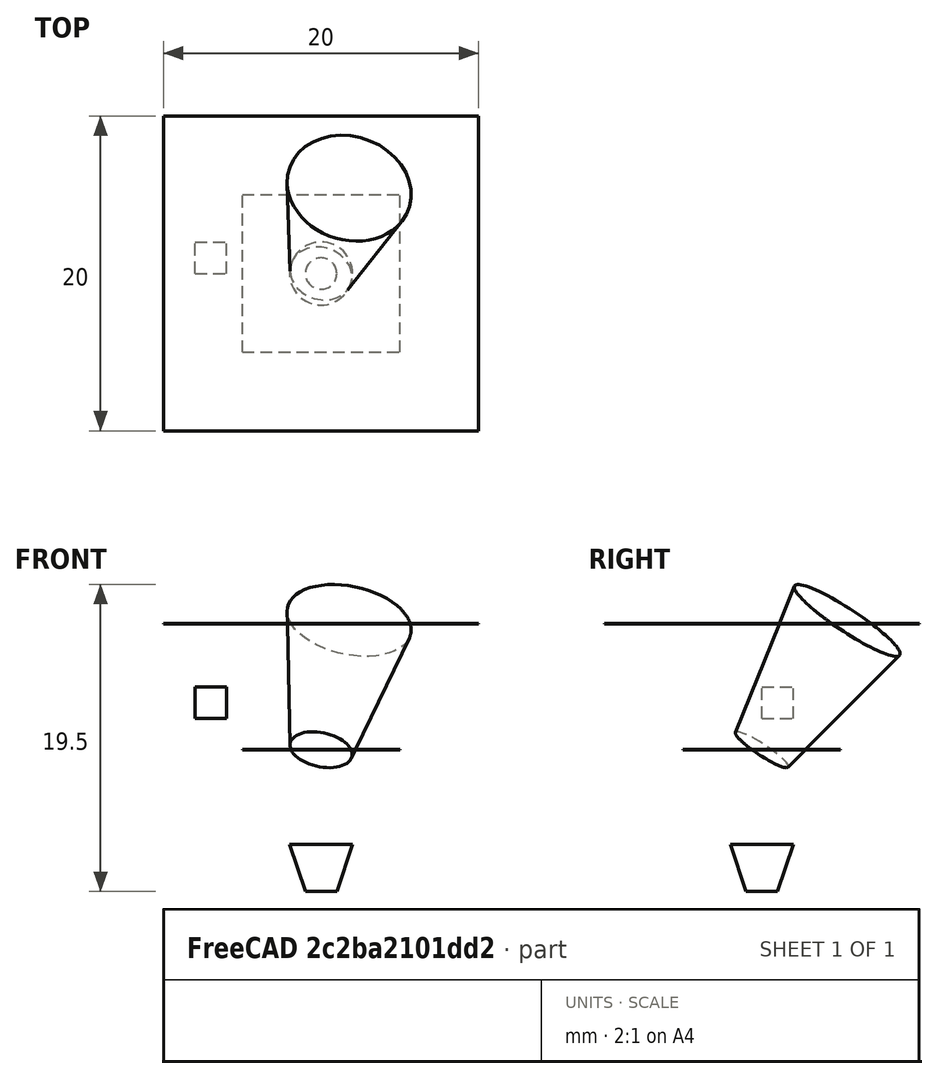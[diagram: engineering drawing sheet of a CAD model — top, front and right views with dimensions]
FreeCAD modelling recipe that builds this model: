
FCSTD DOCUMENT  (FreeCAD 0.16R5332 (Git))
Label: clipping
License: All rights reserved
LicenseURL: http://en.wikipedia.org/wiki/All_rights_reserved
objects: Raytracing::RayFeature×5, Raytracing::LuxFeature×5, Part::Box×3, Part::Cone×2, Raytracing::RayProject×1, Raytracing::LuxProject×1
note: 5 computed .brp shape members not serialized (recipe doc carries the construction recipe); baked Part::Feature solids carry a one-line shape summary decoded from their .brp

FEATURE [Part::Cone] Cone  label="Cono"
  Angle = 360
  Height = 10
  Placement = pos=(0,0,0) rot=(-0.707107,0,-0.707107;0.872665rad)
  Radius1 = 2
  Radius2 = 4
FEATURE [Part::Box] Box  label="Cubo"
  Height = 2
  Length = 2
  Placement = pos=(-8,0,2) rot=(0,0,1;0rad)
  Width = 2
FEATURE [Part::Box] Box001  label="Cubo001"
  Height = 0.01
  Length = 10
  Placement = pos=(-5,-5,0) rot=(0,0,1;0rad)
  Width = 10
FEATURE [Part::Box] Box002  label="Cubo002"
  Height = 0.01
  Length = 20
  Placement = pos=(-10,-10,8) rot=(0,0,1;0rad)
  Width = 20
FEATURE [Part::Cone] Cone001  label="Cono001"
  Angle = 360
  Height = 3
  Placement = pos=(0,0,-9) rot=(0,0,1;0rad)
  Radius1 = 1
  Radius2 = 2
FEATURE [Raytracing::RayFeature] Cone_View
  Result = <blob: 29372 chars omitted>
  Source = -> Cone
  Transparency = 0
FEATURE [Raytracing::RayFeature] Box_View
  Result = <blob: 2592 chars omitted>
  Source = -> Box
  Transparency = 0
FEATURE [Raytracing::RayFeature] Box002_View
  Result = <blob: 2725 chars omitted>
  Source = -> Box002
  Transparency = 90
FEATURE [Raytracing::RayFeature] Box001_View
  Result = <blob: 2677 chars omitted>
  Source = -> Box001
  Transparency = 90
FEATURE [Raytracing::RayFeature] Cone001_View
  Result = <blob: 27672 chars omitted>
  Source = -> Cone001
  Transparency = 0
FEATURE [Raytracing::RayProject] PovProject
  Camera = // declares positon and view direction\n\n// Generated by FreeCAD (http://www.freecadweb.org/)\n#declare cam_location =  <8.61981,-2.10922,-14.3453>;\n#declare cam_look_at  = <-0.356234,6.25966,0.0233555>;\n#declare cam_sky      = <-0.641916,0.416669,-0.643686>;\n#declare cam_angle    = 45; \ncamera {\n  location  cam_location\n  look_at   cam_look_at\n  sky       cam_sky\n  angle     cam_angle \n  right x*800/600\n}
  Group = -> [Cone_View,Box_View,Box002_View,Box001_View,Cone001_View]
FEATURE [Raytracing::LuxFeature] Cone001_View001
  Result = <blob: 19723 chars omitted>
  Source = -> Cone001
  Transparency = 0
FEATURE [Raytracing::LuxFeature] Box_View001
  Result = MakeNamedMaterial "FreeCADMaterial_Lux_Box"\n    "color Kd" [0.8 0.8 0.8]\n    "float sigma" [0.000000000000000]\n    "string type" ["matte"]\n\nAttributeBegin #  "Lux_Box"\nTransform [1 0 0 0 0 1 0 0 0 0 1 0 0 0 0 1]\nNamedMaterial "FreeCADMaterial_Lux_Box"\nShape "mesh"\n    "integer triindices" [3 2 1 0 3 1 5 6 7 5 7 4 9 8 10 8 11 10 14 12 13 14 15 12 17 16 18 16 19 18 22 20 21 22 23 20 ]\n    "point P" [-8 0 2 -8 0 4 -8 2 4 -8 2 2 -6 0 2 -6 0 4 -6 2 4 -6 2 2 -8 0 2 -6 0 2 -6 0 4 -8 0 4 -8 2 2 -6 2 2 -6 2 4 -8 2 4 -8 0 2 -8 2 2 -6 2 2 -6 0 2 -8 0 4 -8 2 4 -6 2 4 -6 0 4 ]\n    "normal N" [-1 -0 0 -1 -0 0 -1 -0 0 -1 -0 0 1 0 -0 1 0 -0 1 0 -0 1 0 -0 -0 -1 -0 -0 -1 -0 -0 -1 -0 -0 -1 -0 0 1 0 0 1 0 0 1 0 0 1 0 -0 -0 -1 -0 -0 -1 -0 -0 -1 -0 -0 -1 0 0 1 0 0 1 0 0 1 0 0 1 ]\n    "bool generatetangents" ["false"]\n    "string name" ["Lux_Box"]\nAttributeEnd # ""
  Source = -> Box
  Transparency = 0
FEATURE [Raytracing::LuxFeature] Cone_View001
  Result = <blob: 21683 chars omitted>
  Source = -> Cone
  Transparency = 0
FEATURE [Raytracing::LuxFeature] Box002_View001
  Result = MakeNamedMaterial "FreeCADMaterial_Base_Lux_Box002"\n    "color Kd" [1 0 0]\n    "float sigma" [0.000000000000000]\n    "string type" ["matte"]\n\nMakeNamedMaterial "FreeCADMaterial_Null_Lux_Box002"\n    "string type" ["null"]\n\nMakeNamedMaterial "FreeCADMaterial_Lux_Box002"\n    "string namedmaterial1" ["FreeCADMaterial_Null_Lux_Box002"]\n    "string namedmaterial2" ["FreeCADMaterial_Base_Lux_Box002"]\n    "float amount" [0.9]\n    "string type" ["mix"]\n\nAttributeBegin #  "Lux_Box002"\nTransform [1 0 0 0 0 1 0 0 0 0 1 0 0 0 0 1]\nNamedMaterial "FreeCADMaterial_Lux_Box002"\nShape "mesh"\n    "integer triindices" [3 2 1 0 3 1 5 6 7 5 7 4 9 8 10 8 11 10 14 12 13 14 15 12 17 16 18 16 19 18 22 20 21 22 23 20 ]\n    "point P" [-10 -10 8 -10 -10 8.01 -10 10 8.01 -10 10 8 10 -10 8 10 -10 8.01 10 10 8.01 10 10 8 -10 -10 8 10 -10 8 10 -10 8.01 -10 -10 8.01 -10 10 8 10 10 8 10 10 8.01 -10 10 8.01 -10 -10 8 -10 10 8 10 10 8 10 -10 8 -10 -10 8.01 -10 10 8.01 10 10 8.01 10 -10 8.01 ]\n    "normal N" [-1 -0 0 -1 -0 0 -1 -0 0 -1 -0 0 1 0 -0 1 0 -0 1 0 -0 1 0 -0 -0 -1 -0 -0 -1 -0 -0 -1 -0 -0 -1 -0 0 1 0 0 1 0 0 1 0 0 1 0 -0 -0 -1 -0 -0 -1 -0 -0 -1 -0 -0 -1 0 0 1 0 0 1 0 0 1 0 0 1 ]\n    "bool generatetangents" ["false"]\n    "string name" ["Lux_Box002"]\nAttributeEnd # ""
  Source = -> Box002
  Transparency = 90
FEATURE [Raytracing::LuxFeature] Box001_View001
  Result = MakeNamedMaterial "FreeCADMaterial_Base_Lux_Box001"\n    "color Kd" [0 0 1]\n    "float sigma" [0.000000000000000]\n    "string type" ["matte"]\n\nMakeNamedMaterial "FreeCADMaterial_Null_Lux_Box001"\n    "string type" ["null"]\n\nMakeNamedMaterial "FreeCADMaterial_Lux_Box001"\n    "string namedmaterial1" ["FreeCADMaterial_Null_Lux_Box001"]\n    "string namedmaterial2" ["FreeCADMaterial_Base_Lux_Box001"]\n    "float amount" [0.9]\n    "string type" ["mix"]\n\nAttributeBegin #  "Lux_Box001"\nTransform [1 0 0 0 0 1 0 0 0 0 1 0 0 0 0 1]\nNamedMaterial "FreeCADMaterial_Lux_Box001"\nShape "mesh"\n    "integer triindices" [3 2 1 0 3 1 5 6 7 5 7 4 9 8 10 8 11 10 14 12 13 14 15 12 17 16 18 16 19 18 22 20 21 22 23 20 ]\n    "point P" [-5 -5 0 -5 -5 0.01 -5 5 0.01 -5 5 0 5 -5 0 5 -5 0.01 5 5 0.01 5 5 0 -5 -5 0 5 -5 0 5 -5 0.01 -5 -5 0.01 -5 5 0 5 5 0 5 5 0.01 -5 5 0.01 -5 -5 0 -5 5 0 5 5 0 5 -5 0 -5 -5 0.01 -5 5 0.01 5 5 0.01 5 -5 0.01 ]\n    "normal N" [-1 -0 0 -1 -0 0 -1 -0 0 -1 -0 0 1 0 -0 1 0 -0 1 0 -0 1 0 -0 -0 -1 -0 -0 -1 -0 -0 -1 -0 -0 -1 -0 0 1 0 0 1 0 0 1 0 0 1 0 -0 -0 -1 -0 -0 -1 -0 -0 -1 -0 -0 -1 0 0 1 0 0 1 0 0 1 0 0 1 ]\n    "bool generatetangents" ["false"]\n    "string name" ["Lux_Box001"]\nAttributeEnd # ""
  Source = -> Box001
  Transparency = 90
FEATURE [Raytracing::LuxProject] LuxProject
  Camera = # declares positon and view direction\n# Generated by FreeCAD (http://www.freecadweb.org/)\nLookAt 14.376 -10.4378 -2.18808 0.217728 1.58815 1.97623 -0.596237 -0.774775 0.210299
  Group = -> [Cone001_View001,Box_View001,Cone_View001,Box002_View001,Box001_View001]
